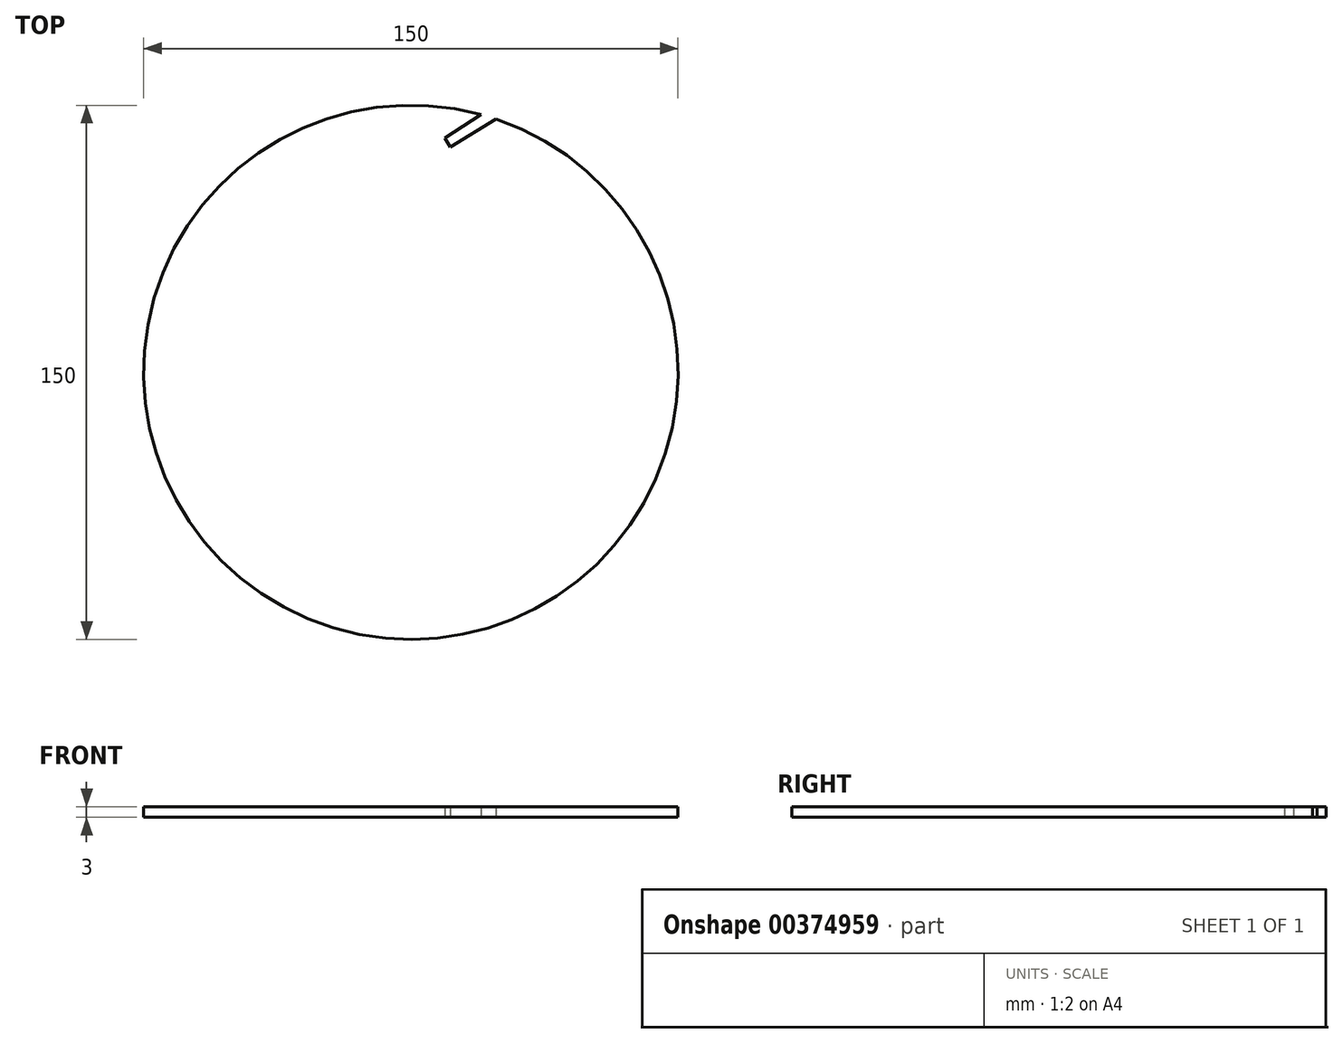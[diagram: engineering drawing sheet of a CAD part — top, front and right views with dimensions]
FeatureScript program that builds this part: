
annotation { "Feature Type Name" : "Feature", "Feature Type Description" : "" }
export const myFeature = defineFeature(function(context is Context, id is Id, definition is map)
    precondition{}
    {
        {
            var Q0;
            Q0=qCreatedBy(makeId("Top.planeOp"),FACE);
            var sketch = newSketch(context, id + "F0", { "sketchPlane" : qUnion([Q0])});
            skCircle(sketch, "E0", {"center": v(0, 0) * mm, "radius": 75 * mm});
            skSolve(sketch);
        }
        {
            var Q0;
            Q0 = qSketchRegion(id + "F0", true);
            extrude(context, id + "F1", {"entities" : qUnion([Q0]), "depth" : 3 * mm});
        }
        {
            var Q0;
            Q0=qCreatedBy(makeId("Top.planeOp"),FACE);
            var sketch = newSketch(context, id + "F2", { "sketchPlane" : qUnion([Q0])});
            skLineSegment(sketch, "E1", {"start": v(28.17, 73.7) * mm, "end": v(11.1, 63.27) * mm});
            skLineSegment(sketch, "E2", {"start": v(11.1, 63.27) * mm, "end": v(9.54, 65.83) * mm});
            skLineSegment(sketch, "E3", {"start": v(9.54, 65.83) * mm, "end": v(19.76, 72.35) * mm});
            skCircle(sketch, "E4", {"center": v(0, 0) * mm, "radius": 75 * mm});
            skLineSegment(sketch, "E5", {"start": v(19.76, 72.35) * mm, "end": v(28.17, 73.7) * mm});
            skSolve(sketch);
        }
        {
            var Q0;
            {var subQ0=sQuery(id+"F2.wireOp",EDGE,"E5");Q0=makeQuery(id+"F2.imprint","IMPRINT",FACE,{"disambiguationData":[TD([[makeQuery(id+"F2.imprint","IMPRINT",EDGE,{"derivedFrom":subQ0}),-1.0]])]});}
            var Q1;
            {var subQ0=sQuery(id+"F2.wireOp",EDGE,"E2");Q1=makeQuery(id+"F2.imprint","IMPRINT",FACE,{"disambiguationData":[TD([[makeQuery(id+"F2.imprint","IMPRINT",EDGE,{"derivedFrom":subQ0}),-1.0]])]});}
            var Q2;
            Q2=makeQuery(id+"F1.opExtrude","CAP_FACE",FACE,{"disambiguationData":[OSD([sQuery(id+"F0.wireOp",EDGE,"E0")])],"isStart":false});
            extrude(context, id + "F3", {"entities" : qUnion([Q0, Q1]), "operationType" : NewBodyOperationType.REMOVE, "endBound" : BoundingType.UP_TO_SURFACE, "endBoundEntityFace" : qUnion([Q2]), "depth" : 3 * mm});
        }
        {
            var Q0;
            Q0=qCreatedBy(makeId("Front.planeOp"),FACE);
            var sketch = newSketch(context, id + "F4", { "sketchPlane" : qUnion([Q0])});
            skLineSegment(sketch, "E6", {"start": v(0, 0) * mm, "end": v(0, 26.35) * mm});
            skSolve(sketch);
        }
    });
